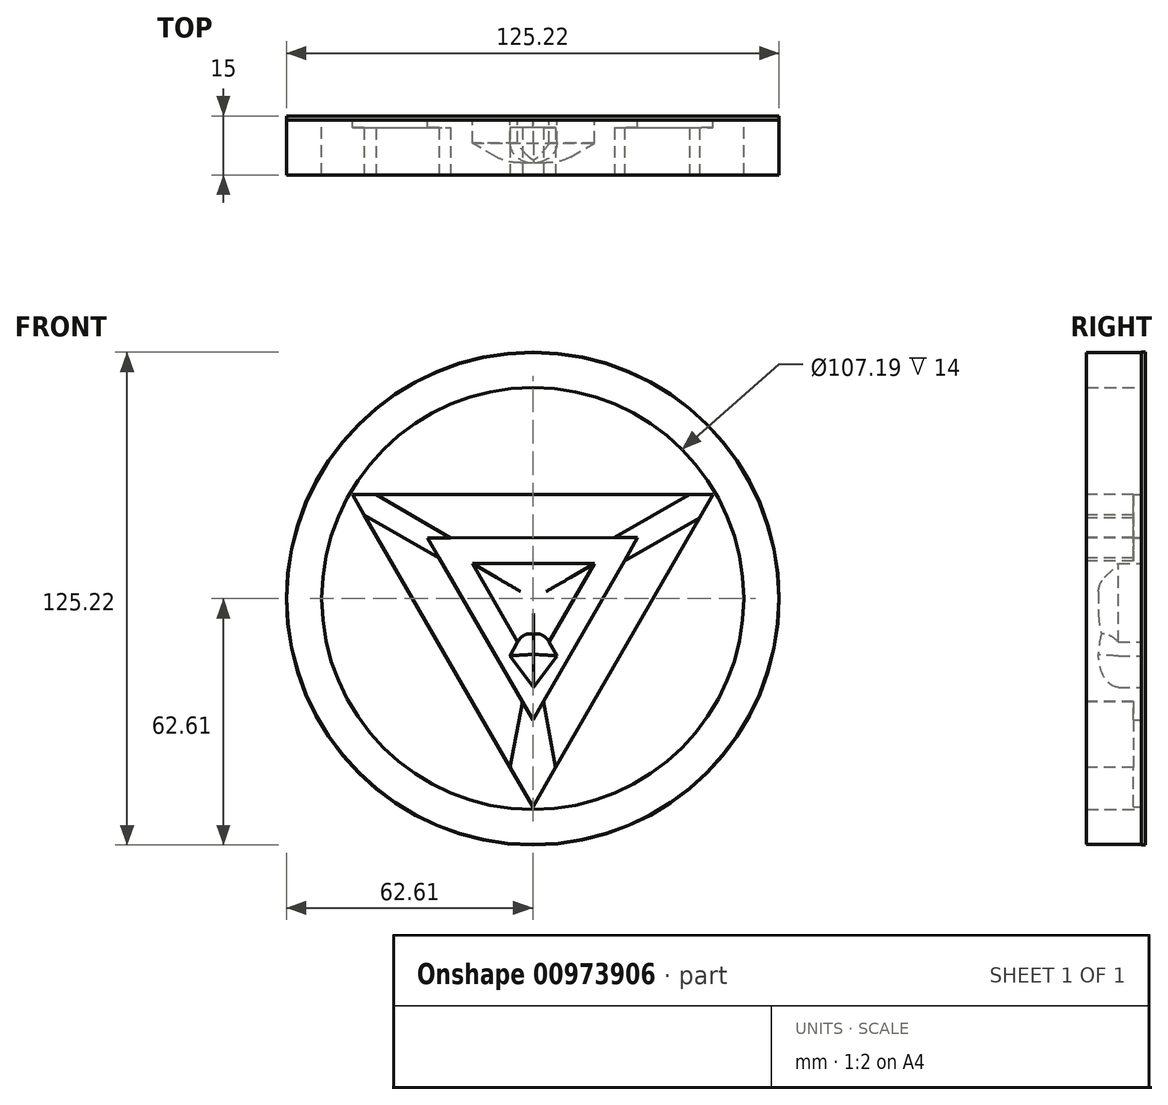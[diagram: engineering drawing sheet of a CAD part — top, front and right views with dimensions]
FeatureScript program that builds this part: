
annotation { "Feature Type Name" : "Feature", "Feature Type Description" : "" }
export const myFeature = defineFeature(function(context is Context, id is Id, definition is map)
    precondition{}
    {
        {
            var Q0;
            Q0=qCreatedBy(makeId("Front.planeOp"),FACE);
            var sketch = newSketch(context, id + "F0", { "sketchPlane" : qUnion([Q0])});
            skCircle(sketch, "E0", {"center": v(0, 0) * mm, "radius": 62.6 * mm});
            skSolve(sketch);
        }
        {
            var Q0;
            Q0=makeQuery(id+"F0.imprint","IMPRINT",FACE,{"disambiguationData":[TD([[makeQuery(id+"F0.imprint","IMPRINT",EDGE,{"derivedFrom":sQuery(id+"F0.wireOp",EDGE,"E0")}),1.0]])]});
            var sketch = newSketch(context, id + "F1", { "sketchPlane" : qUnion([Q0])});
            skCircle(sketch, "E1", {"center": v(0, 0) * mm, "radius": 62.5 * mm});
            skCircle(sketch, "E2", {"center": v(0, 0) * mm, "radius": 53.6 * mm});
            skSolve(sketch);
        }
        {
            var Q0;
            Q0=makeQuery(id+"F0.imprint","IMPRINT",FACE,{"disambiguationData":[TD([[makeQuery(id+"F0.imprint","IMPRINT",EDGE,{"derivedFrom":sQuery(id+"F0.wireOp",EDGE,"E0")}),1.0]])]});
            var sketch = newSketch(context, id + "F2", { "sketchPlane" : qUnion([Q0])});
            skCircle(sketch, "E3.cCircle", {"center": v(0, 0) * mm, "radius": 26.46 * mm, "construction": true});
            skLineSegment(sketch, "E3.0", {"start": v(0, -52.91) * mm, "end": v(-45.82, 26.46) * mm});
            skLineSegment(sketch, "E3.1", {"start": v(-45.82, 26.46) * mm, "end": v(45.82, 26.46) * mm});
            skLineSegment(sketch, "E3.2", {"start": v(45.82, 26.46) * mm, "end": v(0, -52.91) * mm});
            skPoint(sketch, "E3.0.midPoint", {"position": v(-22.91, -13.23) * mm});
            skCircle(sketch, "E4.cCircle", {"center": v(0, 0) * mm, "radius": 15.4 * mm, "construction": true});
            skLineSegment(sketch, "E4.0", {"start": v(26.63, 15.47) * mm, "end": v(0.08, -30.8) * mm});
            skLineSegment(sketch, "E4.1", {"start": v(0.08, -30.8) * mm, "end": v(-26.71, 15.33) * mm});
            skLineSegment(sketch, "E4.2", {"start": v(-26.71, 15.33) * mm, "end": v(26.63, 15.47) * mm});
            skPoint(sketch, "E4.0.midPoint", {"position": v(13.36, -7.66) * mm});
            skSolve(sketch);
        }
        {
            var Q0;
            Q0 = qSketchRegion(id + "F0", true);
            extrude(context, id + "F3", {"entities" : qUnion([Q0]), "depth" : 1 * mm, "offsetDistance" : 25 * mm});
        }
        {
            var Q0;
            Q0 = qSketchRegion(id + "F1", true);
            extrude(context, id + "F4", {"entities" : qUnion([Q0]), "operationType" : NewBodyOperationType.ADD, "depth" : 15 * mm, "offsetDistance" : 25 * mm});
        }
        {
            var Q0;
            Q0 = qSketchRegion(id + "F2", true);
            extrude(context, id + "F5", {"entities" : qUnion([Q0]), "operationType" : NewBodyOperationType.ADD, "depth" : 15 * mm, "offsetDistance" : 25 * mm});
        }
        {
            var Q0;
            Q0=makeQuery(id+"F5.boolean.opBoolean","SPLIT",FACE,{"disambiguationData":[TD([makeQuery(id+"F5.opExtrude","SWEPT_FACE",FACE,{"disambiguationData":[OSD([sQuery(id+"F2.wireOp",EDGE,"E4.0")])]})])],"derivedFrom":makeQuery(id+"F4.boolean.opBoolean","SPLIT",FACE,{"disambiguationData":[TD([makeQuery(id+"F4.opExtrude","SWEPT_FACE",FACE,{"disambiguationData":[OSD([sQuery(id+"F1.wireOp",EDGE,"E2")])]})])],"derivedFrom":makeQuery(id+"F3.opExtrude","CAP_FACE",FACE,{"disambiguationData":[OSD([sQuery(id+"F0.wireOp",EDGE,"E0")])],"isStart":false})})});
            var sketch = newSketch(context, id + "F6", { "sketchPlane" : qUnion([Q0])});
            skCircle(sketch, "E5.cCircle", {"center": v(0, 0) * mm, "radius": 8.85 * mm, "construction": true});
            skLineSegment(sketch, "E5.2", {"start": v(-15.35, 8.85) * mm, "end": v(15.65, 8.85) * mm});
            skPoint(sketch, "E5.0.midPoint", {"position": v(7.67, -4.43) * mm});
            skLineSegment(sketch, "E6", {"start": v(-3.85, -11.07) * mm, "end": v(-5.84, -14.54) * mm});
            skLineSegment(sketch, "E7", {"start": v(-5.84, -14.54) * mm, "end": v(0.15, -22.54) * mm});
            skLineSegment(sketch, "E8", {"start": v(0.15, -22.54) * mm, "end": v(6.14, -14.54) * mm});
            skLineSegment(sketch, "E9", {"start": v(6.14, -14.54) * mm, "end": v(4.15, -11.07) * mm});
            skLineSegment(sketch, "E10", {"start": v(-15.35, 8.85) * mm, "end": v(-3.85, -11.07) * mm});
            skLineSegment(sketch, "E11", {"start": v(4.15, -11.07) * mm, "end": v(15.65, 8.85) * mm});
            skSolve(sketch);
        }
        {
            var Q0;
            Q0=makeQuery(id+"F6.imprint","IMPRINT",FACE,{"disambiguationData":[TD([[makeQuery(id+"F6.imprint","IMPRINT",EDGE,{"derivedFrom":sQuery(id+"F6.wireOp",EDGE,"E5.2")}),-1.0]])]});
            extrude(context, id + "F7", {"entities" : qUnion([Q0]), "operationType" : NewBodyOperationType.ADD, "depth" : 10.9 * mm, "offsetDistance" : 25 * mm});
        }
        {
            var Q0;
            Q0=makeQuery(id+"F5.opExtrude","CAP_FACE",FACE,{"disambiguationData":[OSD([sQuery(id+"F2.wireOp",EDGE,"E3.0"),sQuery(id+"F2.wireOp",EDGE,"E3.1"),sQuery(id+"F2.wireOp",EDGE,"E3.2"),sQuery(id+"F2.wireOp",EDGE,"E4.0"),sQuery(id+"F2.wireOp",EDGE,"E4.1"),sQuery(id+"F2.wireOp",EDGE,"E4.2")])],"isStart":false});
            var sketch = newSketch(context, id + "F8", { "sketchPlane" : qUnion([Q0])});
            skLineSegment(sketch, "E12", {"start": v(-42.82, 21.26) * mm, "end": v(-23.77, 10.27) * mm});
            skLineSegment(sketch, "E13", {"start": v(-39.82, 26.46) * mm, "end": v(-20.84, 15.34) * mm});
            skLineSegment(sketch, "E14", {"start": v(20.77, 15.45) * mm, "end": v(39.82, 26.46) * mm});
            skLineSegment(sketch, "E15", {"start": v(23.24, 9.57) * mm, "end": v(42.36, 20.46) * mm});
            skLineSegment(sketch, "E16", {"start": v(-2.58, -26.22) * mm, "end": v(-5.77, -42.91) * mm});
            skLineSegment(sketch, "E17", {"start": v(2.72, -26.19) * mm, "end": v(5.77, -42.91) * mm});
            skSolve(sketch);
        }
        {
            var Q0;
            {var subQ4=sQuery(id+"F8.wireOp",EDGE,"E12");Q0=makeQuery(id+"F8.imprint","IMPRINT",FACE,{"disambiguationData":[TD([[makeQuery(id+"F8.imprint","IMPRINT",EDGE,{"derivedFrom":subQ4}),1.0]])]});}
            var Q1;
            {var subQ3=sQuery(id+"F8.wireOp",EDGE,"E14");Q1=makeQuery(id+"F8.imprint","IMPRINT",FACE,{"disambiguationData":[TD([[makeQuery(id+"F8.imprint","IMPRINT",EDGE,{"derivedFrom":subQ3}),-1.0]])]});}
            var Q2;
            {var subQ4=sQuery(id+"F8.wireOp",EDGE,"E16");Q2=makeQuery(id+"F8.imprint","IMPRINT",FACE,{"disambiguationData":[TD([[makeQuery(id+"F8.imprint","IMPRINT",EDGE,{"derivedFrom":subQ4}),1.0]])]});}
            extrude(context, id + "F9", {"entities" : qUnion([Q0, Q1, Q2]), "operationType" : NewBodyOperationType.REMOVE, "oppositeDirection" : true, "depth" : 12 * mm, "offsetDistance" : 25 * mm});
        }
        {
            var Q0;
            Q0=makeQuery(id+"F7.opExtrude","CAP_EDGE",EDGE,{"disambiguationData":[OSD([sQuery(id+"F6.wireOp",EDGE,"E11")])],"isStart":false});
            chamfer(context, id + "F10", {"entities" : qUnion([Q0]), "width" : 5 * mm, "tangentPropagation" : true});
        }
        {
            var Q0;
            Q0=makeQuery(id+"F7.opExtrude","CAP_EDGE",EDGE,{"disambiguationData":[OSD([sQuery(id+"F6.wireOp",EDGE,"E10")])],"isStart":false});
            var Q1;
            Q1=makeQuery(id+"F7.opExtrude","CAP_EDGE",EDGE,{"disambiguationData":[OSD([sQuery(id+"F6.wireOp",EDGE,"E5.2")])],"isStart":false});
            chamfer(context, id + "F11", {"entities" : qUnion([Q0, Q1]), "width" : 5 * mm, "tangentPropagation" : true});
        }
        {
            var Q0;
            Q0=makeQuery(id+"F7.opExtrude","CAP_FACE",FACE,{"disambiguationData":[OSD([sQuery(id+"F6.wireOp",EDGE,"E5.2"),sQuery(id+"F6.wireOp",EDGE,"E6"),sQuery(id+"F6.wireOp",EDGE,"E7"),sQuery(id+"F6.wireOp",EDGE,"E8"),sQuery(id+"F6.wireOp",EDGE,"E9"),sQuery(id+"F6.wireOp",EDGE,"E10"),sQuery(id+"F6.wireOp",EDGE,"E11")])],"isStart":false});
            fillet(context, id + "F12", {"entities" : qUnion([Q0]), "radius" : 5 * mm, "tangentPropagation" : true, "allowEdgeOverflow" : false});
        }
    });
